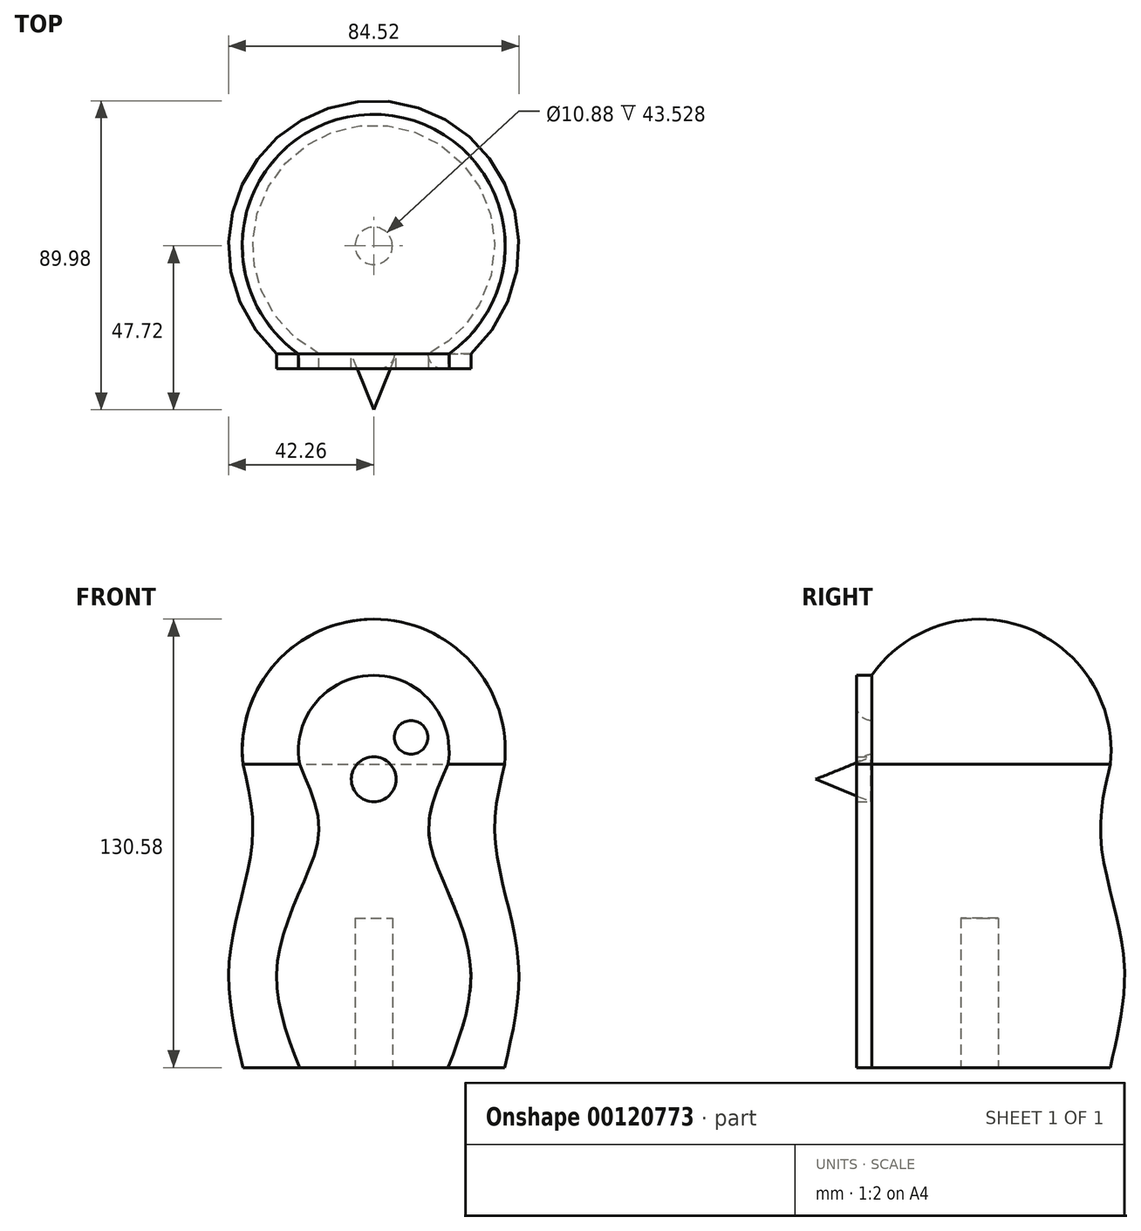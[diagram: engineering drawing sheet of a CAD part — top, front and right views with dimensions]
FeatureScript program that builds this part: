
annotation { "Feature Type Name" : "Feature", "Feature Type Description" : "" }
export const myFeature = defineFeature(function(context is Context, id is Id, definition is map)
    precondition{}
    {
        {
            var Q0;
            Q0=qCreatedBy(makeId("Front.planeOp"),FACE);
            var sketch = newSketch(context, id + "F0", { "sketchPlane" : qUnion([Q0])});
            skLineSegment(sketch, "E0", {"start": v(0, 0) * mm, "end": v(-44.47, 0) * mm});
            skFitSpline(sketch, "E1", {"points": [v(-44.47, 0) * mm, v(-49.12, 36.1) * mm, v(-41.3, 76.56) * mm, v(-44.47, 103.09) * mm], "startDerivative": vector(-23.18, 103.05) * mm, "endDerivative": vector(-19.66, 84.12) * mm});
            skArc(sketch, "E2", {"start": v(0, 152.4) * mm, "mid": v(-33.2, 137.63) * mm, "end": v(-44.47, 103.09) * mm});
            skLineSegment(sketch, "E3", {"start": v(0, 0) * mm, "end": v(0, 152.4) * mm});
            skPoint(sketch, "E4.orphan", {"position": v(44.47, 103.09) * mm});
            skLineSegment(sketch, "E5", {"start": v(-44.47, 103.09) * mm, "end": v(-44.47, 0) * mm, "construction": true});
            skPoint(sketch, "E6", {"position": v(-44.47, 59.82) * mm});
            skPoint(sketch, "E7", {"position": v(-41.15, 83.36) * mm});
            skPoint(sketch, "E8", {"position": v(-49.02, 24.5) * mm});
            skLineSegment(sketch, "E9.left", {"start": v(-44.47, 0) * mm, "end": v(-44.47, -6.35) * mm, "construction": true});
            skFitSpline(sketch, "E10.0", {"points": [v(-38.27, 1.4) * mm, v(-38.76, 3.56) * mm, v(-39.75, 7.85) * mm, v(-41.11, 14.14) * mm, v(-42.2, 20.33) * mm, v(-42.78, 25.45) * mm, v(-42.98, 29.55) * mm, v(-42.97, 32.11) * mm, v(-42.89, 34.18) * mm, v(-42.78, 35.73) * mm, v(-42.63, 37.3) * mm, v(-42.37, 39.44) * mm, v(-41.94, 42.18) * mm, v(-41.08, 46.69) * mm, v(-39.74, 52.48) * mm, v(-37.97, 59.57) * mm, v(-36.6, 65.52) * mm, v(-35.7, 70.27) * mm, v(-35.27, 73.23) * mm, v(-35, 75.6) * mm, v(-34.82, 77.96) * mm, v(-34.72, 80.84) * mm, v(-34.8, 84.17) * mm, v(-35.04, 87.38) * mm, v(-35.4, 90.49) * mm, v(-36.04, 94.48) * mm, v(-37.03, 99.23) * mm, v(-37.88, 102.8) * mm, v(-38.28, 104.53) * mm]});
            skArc(sketch, "E10.1", {"start": v(0, 146.05) * mm, "mid": v(-28.35, 133.52) * mm, "end": v(-38.19, 104.13) * mm});
            skLineSegment(sketch, "E11", {"start": v(-44.47, -6.35) * mm, "end": v(-6.35, -6.35) * mm, "construction": true});
            skLineSegment(sketch, "E12", {"start": v(-6.35, -6.35) * mm, "end": v(0, -6.35) * mm, "construction": true});
            skLineSegment(sketch, "E13", {"start": v(-6.35, -6.35) * mm, "end": v(-6.35, 0) * mm, "construction": true});
            skLineSegment(sketch, "E14", {"start": v(-38.27, 1.4) * mm, "end": v(-38.27, 0) * mm});
            skSolve(sketch);
        }
        {
            var Q0;
            Q0=qSketchRegion(id+"F0",true);
            var Q1;
            Q1=sQuery(id+"F0.wireOp",EDGE,"E3");
            revolve(context, id + "F1", {"entities" : qUnion([Q0]), "axis" : qUnion([Q1]), "revolveType" : RevolveType.FULL});
        }
        {
            var Q0;
            Q0=qCreatedBy(makeId("Top.planeOp"),FACE);
            var sketch = newSketch(context, id + "F2", { "sketchPlane" : qUnion([Q0])});
            skCircle(sketch, "E15", {"center": v(0, 0) * mm, "radius": 44.7 * mm, "construction": true});
            skCircle(sketch, "E16.0", {"center": v(0, 0) * mm, "radius": 44.47 * mm, "construction": true});
            skLineSegment(sketch, "E17", {"start": v(0, 0) * mm, "end": v(0, -44.47) * mm, "construction": true});
            skLineSegment(sketch, "E18", {"start": v(-25.2, -36.64) * mm, "end": v(25.6, -36.64) * mm});
            skLineSegment(sketch, "E19", {"start": v(-25.2, -36.64) * mm, "end": v(-46.78, -36.64) * mm});
            skLineSegment(sketch, "E20.bottom", {"start": v(-46.78, -36.64) * mm, "end": v(42.12, -36.64) * mm});
            skLineSegment(sketch, "E20.top", {"start": v(-46.78, -67.12) * mm, "end": v(42.12, -67.12) * mm});
            skLineSegment(sketch, "E20.left", {"start": v(-46.78, -36.64) * mm, "end": v(-46.78, -67.12) * mm});
            skLineSegment(sketch, "E20.right", {"start": v(42.12, -36.64) * mm, "end": v(42.12, -67.12) * mm});
            skSolve(sketch);
        }
        {
            var Q0;
            Q0=qSketchRegion(id+"F2",true);
            extrude(context, id + "F3", {"entities" : qUnion([Q0]), "operationType" : NewBodyOperationType.REMOVE, "depth" : 177.8 * mm});
        }
        {
            var Q0;
            Q0=makeQuery(id+"F3.boolean.opBoolean","COPY",FACE,{"derivedFrom":makeQuery(id+"F3.opExtrude","SWEPT_FACE",FACE,{"disambiguationData":[OSD([sQuery(id+"F2.wireOp",EDGE,"E20.bottom")])]})});
            var sketch = newSketch(context, id + "F4", { "sketchPlane" : qUnion([Q0])});
            skLineSegment(sketch, "E21", {"start": v(0, 0) * mm, "end": v(0, 133.3) * mm, "construction": true});
            skPoint(sketch, "E22", {"position": v(0, 112.22) * mm});
            skLineSegment(sketch, "E23", {"start": v(-12.7, 112.22) * mm, "end": v(12.7, 112.22) * mm, "construction": true});
            skCircle(sketch, "E24", {"center": v(-12.7, 112.22) * mm, "radius": 5.72 * mm});
            skCircle(sketch, "E25", {"center": v(0, 98) * mm, "radius": 7.62 * mm});
            skCircle(sketch, "E26.MirrorC", {"center": v(12.7, 112.22) * mm, "radius": 5.72 * mm});
            skLineSegment(sketch, "E27", {"start": v(-12.7, 106.5) * mm, "end": v(-12.7, 112.22) * mm, "construction": true});
            skLineSegment(sketch, "E28", {"start": v(-12.7, 112.22) * mm, "end": v(-12.7, 117.94) * mm, "construction": true});
            skSolve(sketch);
        }
        {
            var Q0;
            Q0=makeQuery(id+"F4.imprint","IMPRINT",FACE,{"disambiguationData":[TD([[makeQuery(id+"F4.imprint","IMPRINT",EDGE,{"derivedFrom":sQuery(id+"F4.wireOp",EDGE,"E25")}),1.0]])]});
            extrude(context, id + "F5", {"entities" : qUnion([Q0]), "operationType" : NewBodyOperationType.ADD, "depth" : 19.05 * mm});
        }
        {
            var Q0;
            Q0=makeQuery(id+"F5.opExtrude","CAP_EDGE",EDGE,{"disambiguationData":[OSD([sQuery(id+"F4.wireOp",EDGE,"E25")])],"isStart":false});
            chamfer(context, id + "F6", {"entities" : qUnion([Q0]), "chamferType" : ChamferType.OFFSET_ANGLE, "width" : 7.62 * mm, "oppositeDirection" : false, "angle" : 68 * degree, "tangentPropagation" : true});
        }
        {
            var Q0;
            Q0=makeQuery(id+"F4.imprint","IMPRINT",FACE,{"disambiguationData":[TD([[makeQuery(id+"F4.imprint","IMPRINT",EDGE,{"derivedFrom":sQuery(id+"F4.wireOp",EDGE,"E24")}),1.0]])]});
            var Q1;
            Q1=makeQuery(id+"F4.imprint","IMPRINT",FACE,{"disambiguationData":[TD([[makeQuery(id+"F4.imprint","IMPRINT",EDGE,{"derivedFrom":sQuery(id+"F4.wireOp",EDGE,"E26.MirrorC")}),-1.0]])]});
            extrude(context, id + "F7", {"entities" : qUnion([Q0, Q1]), "operationType" : NewBodyOperationType.ADD, "depth" : 5.08 * mm});
        }
        {
            var Q0;
            Q0=makeQuery(id+"F7.opExtrude","CAP_EDGE",EDGE,{"disambiguationData":[OSD([sQuery(id+"F4.wireOp",EDGE,"E24")])],"isStart":false});
            var Q1;
            Q1=makeQuery(id+"F7.opExtrude","CAP_EDGE",EDGE,{"disambiguationData":[OSD([sQuery(id+"F4.wireOp",EDGE,"E26.MirrorC")])],"isStart":false});
            fillet(context, id + "F8", {"entities" : qUnion([Q0, Q1]), "radius" : 5.08 * mm, "tangentPropagation" : true, "allowEdgeOverflow" : false});
        }
        {
            var Q0;
            Q0=makeQuery(id+"F1.opRevolve","SWEPT_FACE",FACE,{"disambiguationData":[OSD([sQuery(id+"F0.wireOp",EDGE,"E0")])]});
            var sketch = newSketch(context, id + "F9", { "sketchPlane" : qUnion([Q0])});
            skCircle(sketch, "E29", {"center": v(0, 0) * mm, "radius": 6.35 * mm});
            skSolve(sketch);
        }
        {
            var Q0;
            Q0=qSketchRegion(id+"F9",true);
            extrude(context, id + "F10", {"entities" : qUnion([Q0]), "operationType" : NewBodyOperationType.REMOVE, "oppositeDirection" : true, "depth" : 50.8 * mm});
        }
        {
            var Q0;
            Q0=makeQuery(id+"F1.opRevolve","SWEPT_BODY",BODY,{"disambiguationData":[OSD([sQuery(id+"F0.wireOp",EDGE,"E0"),sQuery(id+"F0.wireOp",EDGE,"E1"),sQuery(id+"F0.wireOp",EDGE,"E2"),sQuery(id+"F0.wireOp",EDGE,"E3"),sQuery(id+"F0.wireOp",EDGE,"E9.left"),sQuery(id+"F0.wireOp",EDGE,"E11"),sQuery(id+"F0.wireOp",EDGE,"E13")])]});
            var Q1;
            Q1=qCreatedBy(makeId("Origin.pointOp"),VERTEX);
            transform(context, id + "F11", {"entities" : qUnion([Q0]), "transformType" : TransformType.SCALE_UNIFORMLY, "scale" : .85684223, "scalePoint" : qUnion([Q1]), "makeCopy" : false});
        }
    });
